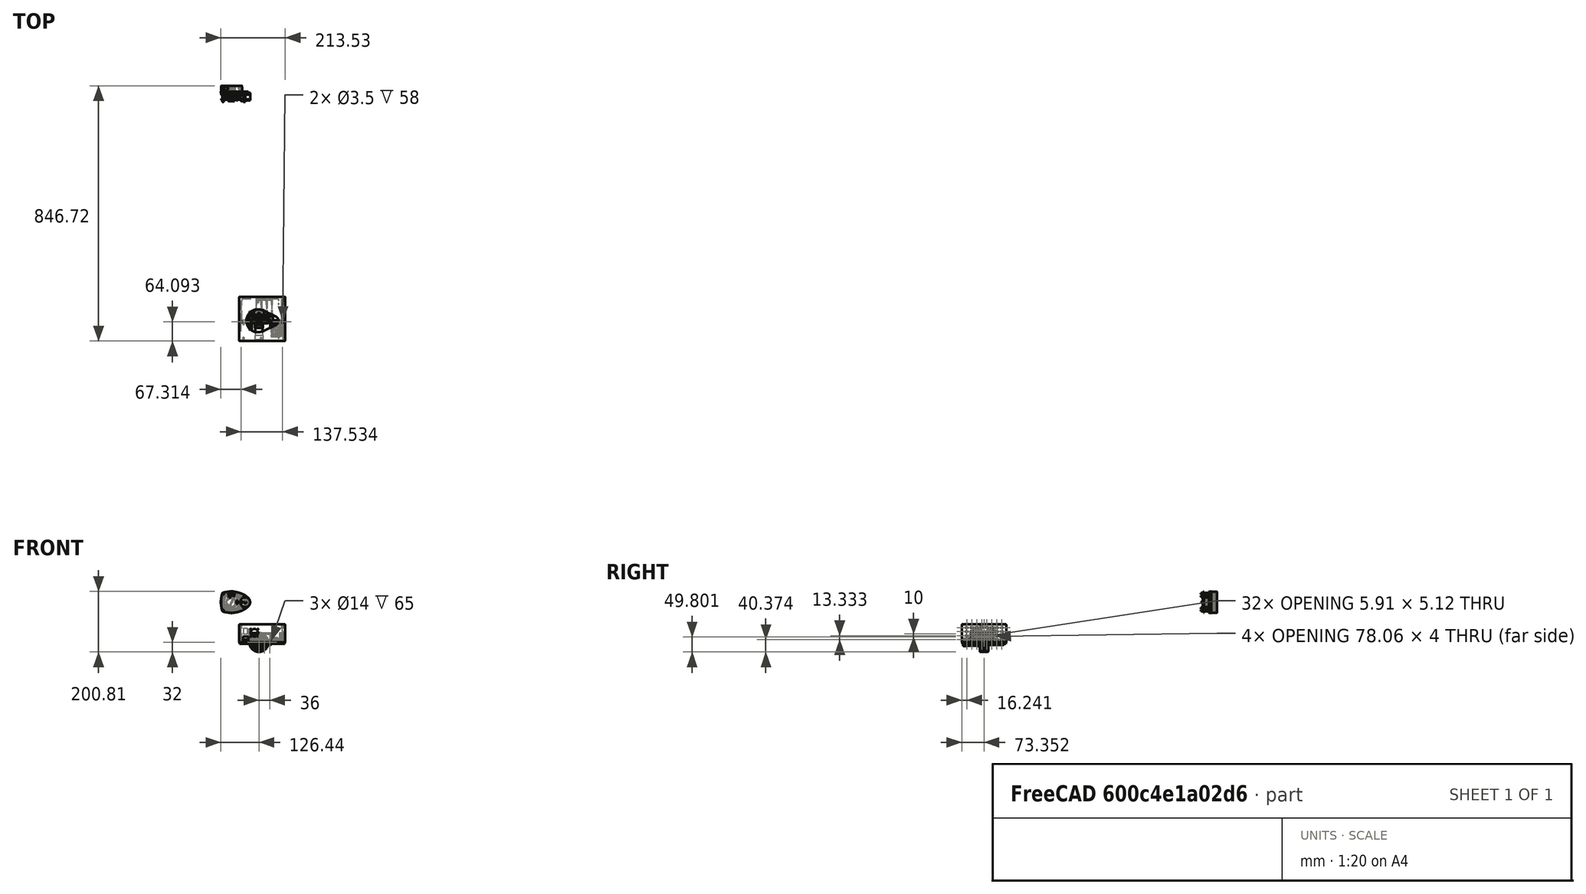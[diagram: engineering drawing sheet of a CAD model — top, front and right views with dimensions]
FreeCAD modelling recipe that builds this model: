
FCSTD DOCUMENT  (FreeCAD 0.20R29603 (Git))
Label: autonomous_bot
License: All rights reserved
LicenseURL: http://en.wikipedia.org/wiki/All_rights_reserved
objects: Part::Feature×53, Sketcher::SketchObject×19, PartDesign::Pad×14, App::Part×13, PartDesign::Pocket×8, PartDesign::Body×4, PartDesign::LinearPattern×3, PartDesign::Fillet×2, PartDesign::MultiTransform×2, Mesh::Feature×1, PartDesign::Plane×1, PartDesign::Thickness×1, PartDesign::Hole×1
note: 134 computed .brp shape members not serialized (recipe doc carries the construction recipe); baked Part::Feature solids carry a one-line shape summary decoded from their .brp

FEATURE [Part::Feature] Part__Feature002  label="cell"
  Placement = pos=(0,0,0) rot=(-1,0,0;1.5708rad)
  shape: bbox 19.5 x 65.01 x 19.5 mm, 44 faces, 4 solids (baked)
FEATURE [Part::Feature] Part__Feature093  label="cell001"
  Placement = pos=(18,0,0) rot=(-1,0,0;1.5708rad)
  shape: bbox 19.5 x 65.01 x 19.5 mm, 44 faces, 4 solids (baked)
FEATURE [Part::Feature] Part__Feature094  label="cell002"
  Placement = pos=(36,0,0) rot=(-1,0,0;1.5708rad)
  shape: bbox 19.5 x 65.01 x 19.5 mm, 44 faces, 4 solids (baked)
FEATURE [Part::Feature] Part__Feature095  label="L298N Motor Driver001"
  Placement = pos=(62,-37,4) rot=(0.57735,0.57735,0.57735;2.0944rad)
  shape: bbox 43.5 x 43.5 x 26 mm, 749 faces, 21 solids (baked)
FEATURE [App::Part] Part002  label="battery"
  Group = -> [Part__Feature094,Part__Feature093,Part__Feature002]
  Origin = -> Origin037
  Placement = pos=(67,23,18) rot=(0,0,1;1.5708rad)
FEATURE [Part::Feature] Part__Feature096  label="1"
  Placement = pos=(0,3,-1e-15) rot=(1,0,0;3.14159rad)
  shape: bbox 27 x 32.5 x 32.1 mm, 22 faces (baked)
FEATURE [Part::Feature] Part__Feature097  label="2"
  Placement = pos=(3e-15,-12,3e-15) rot=(0,0,1;0rad)
  shape: bbox 26.5 x 69.5 x 26.5 mm, 11 faces (baked)
FEATURE [App::Part] _  label="3"
  Group = -> [Part__Feature096,Part__Feature097]
  Origin = -> Origin039
FEATURE [Part::Feature] Part__Feature098  label="4"
  shape: bbox 52 x 26 x 52 mm, 199 faces (baked)
FEATURE [Part::Feature] Part__Feature099  label="5"
  Placement = pos=(-1e-15,0,-4e-15) rot=(0,1,0;0.005059rad)
  shape: bbox 73.6 x 28 x 73.6 mm, 536 faces (baked)
FEATURE [App::Part] _001  label="6"
  Group = -> [Part__Feature098,Part__Feature099]
  Origin = -> Origin040
FEATURE [Part::Feature] Part__Feature100  label="7"
  Placement = pos=(0,-14,0) rot=(0,0,1;0rad)
  shape: bbox 13 x 26 x 15.01 mm, 12 faces (baked)
FEATURE [Part::Feature] Part__Feature101  label="<unrecoverable-encoding: 39 bytes e8eeb0a0f2aca1b1ebb1b3e4... md5=072de469>7045 - ʳ x 6 - H"
  Placement = pos=(4,-22,6.9282) rot=(0.047005,0.995571,-0.081416;2.09823rad)
  shape: bbox 7.624 x 5.981 x 8.776 mm, 28 faces (baked)
FEATURE [Part::Feature] Part__Feature102  label="Âèíò ñ öèëèíäðè÷åñêîé ãîëîâêîé è øåñòèãðàííûì óãëóáëåíèåì ïîä êëþ÷ ÃÎÑÒ Ð ÈÑÎ 4762 - Ì3 x 12"
  Placement = pos=(0,6.5,0) rot=(0,0,-1;1.5708rad)
  shape: bbox 5.953 x 15 x 5.953 mm, 15 faces (baked)
FEATURE [Part::Feature] Part__Feature103  label="10"
  Placement = pos=(0,-31,0) rot=(0,0,1;0rad)
  shape: bbox 4 x 15 x 4 mm, 3 faces (baked)
FEATURE [App::Part] _1  label="11"
  Group = -> [_001,Part__Feature100,Part__Feature101,Part__Feature102,Part__Feature103]
  Origin = -> Origin041
  Placement = pos=(4e-16,31,-6.6e-15) rot=(0,1,0;1.91042rad)
FEATURE [App::Part] Shapes  label="motor_wheel_r"
  Group = -> [_,_1]
  Origin = -> Origin042
  Placement = pos=(71.52,71,-23.51) rot=(0,1,0;6.28318rad)
FEATURE [Mesh::Feature] Raspberry_Pi_4_Model_B_03  label="Raspberry_Pi_4-Model_B-03"
  Placement = pos=(-12,-40,4) rot=(0,0,1;0rad)
FEATURE [Part::Feature] RP_lidar_A1
  Placement = pos=(-90.5533,748.292,132.918) rot=(0,0,1;0rad)
  shape: bbox 114.9 x 12.7 x 93.34 mm, 1511 faces (baked)
FEATURE [Part::Feature] RP_lidar_A1001
  Placement = pos=(-90.5533,751.292,132.918) rot=(0,1,0;0.450629rad)
  shape: bbox 106.3 x 21.41 x 108.5 mm, 315 faces (baked)
FEATURE [Part::Feature] RP_lidar_A1002
  Placement = pos=(-90.4238,754.292,132.776) rot=(0,1,0;2.02364rad)
  shape: bbox 32 x 21.09 x 28.13 mm, 95 faces (baked)
FEATURE [Part::Feature] RP_lidar_A1003
  Placement = pos=(-93.3269,763.292,153.094) rot=(-0.486868,-0.396432,0.778332;2.01185rad)
  shape: bbox 17.19 x 18.52 x 19.42 mm, 10 faces (baked)
FEATURE [Part::Feature] RP_lidar_A1004
  Placement = pos=(-96.1268,764.292,107.826) rot=(-0.316381,-0.743803,0.588778;1.25125rad)
  shape: bbox 22.76 x 9.219 x 19.38 mm, 14 faces (baked)
FEATURE [Part::Feature] RP_lidar_A1005
  Placement = pos=(-90.5533,755.292,132.918) rot=(0,1,0;2.01581rad)
  shape: bbox 22.94 x 18.5 x 22.57 mm, 35 faces (baked)
FEATURE [Part::Feature] RP_lidar_A1006
  Placement = pos=(-90.5533,773.192,132.918) rot=(0.847211,0,0.531257;3.14159rad)
  shape: bbox 106.3 x 19.54 x 108.3 mm, 453 faces (baked)
FEATURE [Part::Feature] RP_lidar_A1007
  Placement = pos=(-64.2029,766.792,142.386) rot=(0.652395,-0.652395,-0.385697;2.40536rad)
  shape: bbox 5.324 x 7.569 x 5.324 mm, 18 faces (baked)
FEATURE [Part::Feature] RP_lidar_A1008
  Placement = pos=(-81.6242,766.792,106.379) rot=(0.652395,-0.652395,-0.385697;2.40536rad)
  shape: bbox 5.324 x 7.569 x 5.324 mm, 18 faces (baked)
FEATURE [Part::Feature] RP_lidar_A1009
  Placement = pos=(-115.758,766.792,145.112) rot=(0.639808,-0.639808,-0.425783;2.33652rad)
  shape: bbox 5.13 x 7.569 x 5.13 mm, 18 faces (baked)
FEATURE [Part::Feature] RP_lidar_A1010
  Placement = pos=(-90.5533,738.292,132.918) rot=(0,0,1;0rad)
  shape: bbox 55.52 x 1.02 x 57.02 mm, 27 faces (baked)
FEATURE [Part::Feature] RP_lidar_A1011
  Placement = pos=(-57.5533,723.492,132.555) rot=(0.57735,-0.57735,0.57735;2.0944rad)
  shape: bbox 5.22 x 3.42 x 8.92 mm, 221 faces (baked)
FEATURE [Part::Feature] RP_lidar_A1012
  Placement = pos=(-45.0533,728.792,132.918) rot=(0,-1,0;1.5708rad)
  shape: bbox 32 x 30.2 x 32.81 mm, 39 faces (baked)
FEATURE [Part::Feature] RP_lidar_A1013
  Placement = pos=(-45.0533,725.192,132.918) rot=(0,-1,0;1.13719rad)
  shape: bbox 42.51 x 1.6 x 42.51 mm, 4 faces (baked)
FEATURE [Part::Feature] RP_lidar_A1014
  Placement = pos=(-45.0533,750.592,121.918) rot=(-0.016461,0.016461,-0.999729;1.57107rad)
  shape: bbox 4.047 x 7.569 x 4.047 mm, 18 faces (baked)
FEATURE [Part::Feature] RP_lidar_A1015
  Placement = pos=(-45.0533,750.592,143.918) rot=(-0.016461,0.016461,-0.999729;1.57107rad)
  shape: bbox 4.047 x 7.569 x 4.047 mm, 18 faces (baked)
FEATURE [Part::Feature] RP_lidar_A1016
  Placement = pos=(-68.3533,736.442,132.793) rot=(0.707107,0,0.707107;3.14159rad)
  shape: bbox 4.72 x 4.22 x 10.17 mm, 257 faces (baked)
FEATURE [Part::Feature] RP_lidar_A1017
  Placement = pos=(-90.5533,737.292,132.918) rot=(0,0,1;0rad)
  shape: bbox 60.22 x 11.07 x 60.95 mm, 180 faces (baked)
FEATURE [Part::Feature] RP_lidar_A1018
  Placement = pos=(-118.553,729.292,160.918) rot=(0,0,1;0rad)
  shape: bbox 5.794 x 15.02 x 5.02 mm, 9 faces (baked)
FEATURE [Part::Feature] RP_lidar_A1019
  Placement = pos=(-48.5533,727.692,152.918) rot=(1,0,0;3.14159rad)
  shape: bbox 5.794 x 8.02 x 5.02 mm, 9 faces (baked)
FEATURE [Part::Feature] RP_lidar_A1020
  Placement = pos=(-48.5533,729.292,152.918) rot=(0,0,1;0rad)
  shape: bbox 5.794 x 15.02 x 5.02 mm, 9 faces (baked)
FEATURE [Part::Feature] RP_lidar_A1021
  Placement = pos=(-118.553,727.692,160.918) rot=(1,0,0;3.14159rad)
  shape: bbox 5.794 x 8.02 x 5.02 mm, 9 faces (baked)
FEATURE [Part::Feature] RP_lidar_A1022
  Placement = pos=(-48.5533,729.292,112.918) rot=(0,0,1;0rad)
  shape: bbox 5.794 x 15.02 x 5.02 mm, 9 faces (baked)
FEATURE [Part::Feature] RP_lidar_A1023
  Placement = pos=(-118.553,727.692,104.918) rot=(1,0,0;3.14159rad)
  shape: bbox 5.794 x 8.02 x 5.02 mm, 9 faces (baked)
FEATURE [Part::Feature] RP_lidar_A1024
  Placement = pos=(-118.553,729.292,104.918) rot=(0,0,1;0rad)
  shape: bbox 5.794 x 15.02 x 5.02 mm, 9 faces (baked)
FEATURE [Part::Feature] RP_lidar_A1025
  Placement = pos=(-48.5533,727.692,112.918) rot=(1,0,0;3.14159rad)
  shape: bbox 5.794 x 8.02 x 5.02 mm, 9 faces (baked)
FEATURE [Part::Feature] RP_lidar_A1026
  Placement = pos=(-90.5533,727.692,160.018) rot=(0.57735,-0.57735,0.57735;4.18879rad)
  shape: bbox 20.02 x 8.21 x 5.02 mm, 42 faces (baked)
FEATURE [Part::Feature] RP_lidar_A1027
  Placement = pos=(-90.5533,729.292,132.918) rot=(1,0,0;3.14159rad)
  shape: bbox 85.12 x 214.2 x 70.02 mm, 368 faces (baked)
FEATURE [Part::Feature] RP_lidar_A1028
  Placement = pos=(-90.5533,751.478,132.918) rot=(1,0,0;1.5708rad)
  shape: bbox 103.2 x 2 x 95.72 mm, 4 faces (baked)
FEATURE [Part::Feature] RP_lidar_A1029
  Placement = pos=(-45.0533,749.292,132.918) rot=(0,1,0;1.69522rad)
  shape: bbox 20.12 x 5.5 x 20.12 mm, 19 faces (baked)
FEATURE [App::Part] Part003  label="RPILIDAR"
  Group = -> [RP_lidar_A1,RP_lidar_A1001,RP_lidar_A1002,RP_lidar_A1003,RP_lidar_A1004,RP_lidar_A1005,RP_lidar_A1006,RP_lidar_A1007,RP_lidar_A1008,RP_lidar_A1009,RP_lidar_A1010,RP_lidar_A1011,RP_lidar_A1012,RP_lidar_A1013,RP_lidar_A1014,RP_lidar_A1015,RP_lidar_A1016,RP_lidar_A1017,RP_lidar_A1018,RP_lidar_A1019,RP_lidar_A1020,RP_lidar_A1021,RP_lidar_A1022,RP_lidar_A1023,RP_lidar_A1024,RP_lidar_A1025,+4 more]
  Origin = -> Origin038
  Placement = pos=(90,127,-691) rot=(1,0,0;1.5708rad)
FEATURE [Part::Feature] Part__Feature104  label="1002"
  Placement = pos=(0,3,-1e-15) rot=(1,0,0;3.14159rad)
  shape: bbox 27 x 32.5 x 32.1 mm, 22 faces (baked)
FEATURE [Part::Feature] Part__Feature105  label="2001"
  Placement = pos=(3e-15,-12,3e-15) rot=(0,0,1;0rad)
  shape: bbox 26.5 x 69.5 x 26.5 mm, 11 faces (baked)
FEATURE [Part::Feature] Part__Feature106  label="4001"
  shape: bbox 52 x 26 x 52 mm, 199 faces (baked)
FEATURE [Part::Feature] Part__Feature107  label="5001"
  Placement = pos=(-1e-15,0,-4e-15) rot=(0,1,0;0.005059rad)
  shape: bbox 73.6 x 28 x 73.6 mm, 536 faces (baked)
FEATURE [Part::Feature] Part__Feature108  label="7001"
  Placement = pos=(0,-14,0) rot=(0,0,1;0rad)
  shape: bbox 13 x 26 x 15.01 mm, 12 faces (baked)
FEATURE [Part::Feature] Part__Feature109  label="<unrecoverable-encoding: 39 bytes e8eeb0a0f2aca1b1ebb1b3e4... md5=072de469>7045 - ʳ x 6 - H001"
  Placement = pos=(4,-22,6.9282) rot=(0.047005,0.995571,-0.081416;2.09823rad)
  shape: bbox 7.624 x 5.981 x 8.776 mm, 28 faces (baked)
FEATURE [Part::Feature] Part__Feature110  label="Âèíò ñ öèëèíäðè÷åñêîé ãîëîâêîé è øåñòèãðàííûì óãëóáëåíèåì ïîä êëþ÷ ÃÎÑÒ Ð ÈÑÎ 4762 - Ì3 x 013"
  Placement = pos=(0,6.5,0) rot=(0,0,-1;1.5708rad)
  shape: bbox 5.953 x 15 x 5.953 mm, 15 faces (baked)
FEATURE [Part::Feature] Part__Feature111  label="10003"
  Placement = pos=(0,-31,0) rot=(0,0,1;0rad)
  shape: bbox 4 x 15 x 4 mm, 3 faces (baked)
FEATURE [App::Part] _002  label="3001"
  Group = -> [Part__Feature104,Part__Feature105]
  Origin = -> Origin043
FEATURE [App::Part] _003  label="6001"
  Group = -> [Part__Feature106,Part__Feature107]
  Origin = -> Origin044
FEATURE [App::Part] _004  label="11001"
  Group = -> [_003,Part__Feature108,Part__Feature109,Part__Feature110,Part__Feature111]
  Origin = -> Origin045
  Placement = pos=(4e-16,31,-6.6e-15) rot=(0,1,0;1.91042rad)
FEATURE [App::Part] Shapes001  label="motor_wheel_l"
  Group = -> [_002,_004]
  Origin = -> Origin046
  Placement = pos=(71,-71,-24.27) rot=(0,0,-1;3.14159rad)
FEATURE [Sketcher::SketchObject] Sketch
  FullyConstrained = true
  MapMode = 5
  Support = -> [XY_Plane048]
  sketch-geometry (4):
    g0: LineSegment StartX=-75 StartY=72.5 StartZ=0 EndX=75 EndY=72.5 EndZ=0
    g1: LineSegment StartX=75 StartY=72.5 StartZ=0 EndX=75 EndY=-72.5 EndZ=0
    g2: LineSegment StartX=75 StartY=-72.5 StartZ=0 EndX=-75 EndY=-72.5 EndZ=0
    g3: LineSegment StartX=-75 StartY=-72.5 StartZ=0 EndX=-75 EndY=72.5 EndZ=0
  constraints (11):
    c: Coincident(g0,g1)
    c: Coincident(g1,g2)
    c: Coincident(g2,g3)
    c: Coincident(g3,g0)
    c: Horizontal(g0)
    c: Horizontal(g2)
    c: Vertical(g1)
    c: Vertical(g3)
    c: Symmetric(g1,g0,g-1)
    c: DistanceX(g0,g0) = 150
    c: DistanceY(g1,g1) = 145
FEATURE [Part::Feature] Part__Feature112  label="Caster_40mm_Wheel_30mm_01"
  shape: bbox 15.6 x 30 x 30 mm, 12 faces (baked)
FEATURE [Part::Feature] Part__Feature113  label="Caster_40mm_Wheel_support_01"
  shape: bbox 25.52 x 33.35 x 25.15 mm, 56 faces (baked)
FEATURE [Part::Feature] Part__Feature114  label="Caster_40mm_Swivel_plate_01"
  shape: bbox 38 x 33.34 x 8.3 mm, 30 faces (baked)
FEATURE [App::Part] Part004  label="Caster Wheel"
  Group = -> [Part__Feature112,Part__Feature113,Part__Feature114]
  Origin = -> Origin049
  Placement = pos=(-33,-1,-42) rot=(0,0,1;1.5708rad)
FEATURE [PartDesign::Pad] Pad
  Direction = (0,0,1)
  Length = 5
  Length2 = 10
  Profile = -> Sketch
  ReferenceAxis = -> Sketch [N_Axis]
  Reversed = true
  Type = 0
FEATURE [Sketcher::SketchObject] Sketch001
  ExternalGeometry = -> [Pad]
  FullyConstrained = false
  MapMode = 5
  Support = -> [Pad]
  sketch-geometry (8):
    g0: Circle CenterX=54 CenterY=63.26 CenterZ=0 NormalX=0 NormalY=0 NormalZ=1 AngleXU=0 Radius=1.51945
    g1: Circle CenterX=69 CenterY=63.26 CenterZ=0 NormalX=0 NormalY=0 NormalZ=1 AngleXU=0 Radius=1.57564
    g2: Circle CenterX=69 CenterY=49.76 CenterZ=0 NormalX=0 NormalY=0 NormalZ=1 AngleXU=0 Radius=1.58481
    g3: Circle CenterX=54 CenterY=49.76 CenterZ=0 NormalX=0 NormalY=0 NormalZ=1 AngleXU=0 Radius=1.46067
    g4: Circle CenterX=54 CenterY=-49.76 CenterZ=0 NormalX=0 NormalY=0 NormalZ=1 AngleXU=0 Radius=1.51945
    g5: Circle CenterX=69 CenterY=-49.76 CenterZ=0 NormalX=0 NormalY=0 NormalZ=1 AngleXU=0 Radius=1.57564
    g6: Circle CenterX=69 CenterY=-63.26 CenterZ=0 NormalX=0 NormalY=0 NormalZ=1 AngleXU=0 Radius=1.58481
    g7: Circle CenterX=54 CenterY=-63.26 CenterZ=0 NormalX=0 NormalY=0 NormalZ=1 AngleXU=0 Radius=1.46067
  constraints (16):
    c: DistanceX(g3,g2) = 15
    c: Vertical(g3,g0)
    c: Horizontal(g2,g3)
    c: Vertical(g2,g1)
    c: DistanceY(g3,g0) = 13.5
    c: DistanceX(g1,g-3) = 6
    c: Horizontal(g0,g1)
    c: DistanceX(g7,g6) = 15
    c: Vertical(g7,g4)
    c: Horizontal(g6,g7)
    c: Vertical(g6,g5)
    c: DistanceY(g7,g4) = 13.5
    c: Horizontal(g4,g5)
    c: Vertical(g5,g2)
    c: DistanceY(g1,g-3) = 9.24
    c: DistanceY(g-4,g6) = 9.24
FEATURE [PartDesign::Pocket] Pocket
  BaseFeature = -> Pad
  Direction = (0,0,-1)
  Length = 5
  Length2 = 5
  Profile = -> Sketch001
  ReferenceAxis = -> Sketch001 [N_Axis]
  Type = 0
FEATURE [Sketcher::SketchObject] Sketch002
  FullyConstrained = false
  MapMode = 5
  Support = -> [XY_Plane050]
  sketch-geometry (4):
    g0: LineSegment StartX=-66.2084 StartY=72.1684 StartZ=0 EndX=63.7916 EndY=72.1684 EndZ=0
    g1: LineSegment StartX=63.7916 StartY=72.1684 StartZ=0 EndX=63.7916 EndY=1.16836 EndZ=0
    g2: LineSegment StartX=63.7916 StartY=1.16836 StartZ=0 EndX=-66.2084 EndY=1.16836 EndZ=0
    g3: LineSegment StartX=-66.2084 StartY=1.16836 StartZ=0 EndX=-66.2084 EndY=72.1684 EndZ=0
  constraints (10):
    c: Coincident(g0,g1)
    c: Coincident(g1,g2)
    c: Coincident(g2,g3)
    c: Coincident(g3,g0)
    c: Horizontal(g0)
    c: Horizontal(g2)
    c: Vertical(g1)
    c: Vertical(g3)
    c: DistanceY(g1,g1) = 71
    c: DistanceX(g0,g0) = 130
FEATURE [PartDesign::Pad] Pad001
  Direction = (0,0,1)
  Length = 9
  Length2 = 10
  Profile = -> Sketch002
  ReferenceAxis = -> Sketch002 [N_Axis]
  Type = 0
FEATURE [PartDesign::Fillet] Fillet
  Base = -> Pad001 [Edge9,Edge10,Edge4,Edge3]
  BaseFeature = -> Pad001
  Radius = 4
  SupportTransform = false
  UseAllEdges = false
FEATURE [PartDesign::Body] Body002  label="Power_bank"
  Group = -> [Sketch002,Pad001,Fillet]
  Origin = -> Origin050
  Placement = pos=(10,-6,0) rot=(0,0,1;0rad)
  Tip = -> Fillet
FEATURE [App::Part] Part001  label="Components"
  Group = -> [Part__Feature095,Part002,Shapes,Raspberry_Pi_4_Model_B_03,Part003,Shapes001,Part004,Body002]
  Origin = -> Origin036
FEATURE [Sketcher::SketchObject] Sketch003
  FullyConstrained = false
  MapMode = 5
  Support = -> [Pocket]
  sketch-geometry (16):
    g0: Circle CenterX=69.7676 CenterY=-18.2699 CenterZ=0 NormalX=0 NormalY=0 NormalZ=1 AngleXU=0 Radius=1.5
    g1: Circle CenterX=69.7676 CenterY=-18.2699 CenterZ=0 NormalX=0 NormalY=0 NormalZ=1 AngleXU=0 Radius=3
    g2: Circle CenterX=32.2561 CenterY=-18.2919 CenterZ=0 NormalX=0 NormalY=0 NormalZ=1 AngleXU=0 Radius=1.5
    g3: Circle CenterX=32.2561 CenterY=-18.2919 CenterZ=0 NormalX=0 NormalY=0 NormalZ=1 AngleXU=0 Radius=3
    g4: Circle CenterX=32.2849 CenterY=-55.7579 CenterZ=0 NormalX=0 NormalY=0 NormalZ=1 AngleXU=0 Radius=1.5
    g5: Circle CenterX=32.2849 CenterY=-55.7579 CenterZ=0 NormalX=0 NormalY=0 NormalZ=1 AngleXU=0 Radius=3
    g6: Circle CenterX=69.7365 CenterY=-55.7732 CenterZ=0 NormalX=0 NormalY=0 NormalZ=1 AngleXU=0 Radius=1.5
    g7: Circle CenterX=69.7365 CenterY=-55.7732 CenterZ=0 NormalX=0 NormalY=0 NormalZ=1 AngleXU=0 Radius=3
    g8: Circle CenterX=-62.0545 CenterY=-15.516 CenterZ=0 NormalX=0 NormalY=0 NormalZ=1 AngleXU=0 Radius=1.5
    g9: Circle CenterX=-62.0545 CenterY=-15.516 CenterZ=0 NormalX=0 NormalY=0 NormalZ=1 AngleXU=0 Radius=3
    g10: Circle CenterX=-4.04448 CenterY=-15.6135 CenterZ=0 NormalX=0 NormalY=0 NormalZ=1 AngleXU=0 Radius=1.5
    g11: Circle CenterX=-4.04448 CenterY=-15.6135 CenterZ=0 NormalX=0 NormalY=0 NormalZ=1 AngleXU=0 Radius=3
    g12: Circle CenterX=-4.04448 CenterY=-64.6735 CenterZ=0 NormalX=0 NormalY=0 NormalZ=1 AngleXU=0 Radius=1.5
    g13: Circle CenterX=-4.04448 CenterY=-64.6735 CenterZ=0 NormalX=0 NormalY=0 NormalZ=1 AngleXU=0 Radius=3
    g14: Circle CenterX=-62.0645 CenterY=-64.556 CenterZ=0 NormalX=0 NormalY=0 NormalZ=1 AngleXU=0 Radius=1.5
    g15: Circle CenterX=-62.0645 CenterY=-64.556 CenterZ=0 NormalX=0 NormalY=0 NormalZ=1 AngleXU=0 Radius=3
  constraints (22):
    c: Coincident(g1,g0)
    c: Diameter(g0) = 3
    c: Coincident(g3,g2)
    c: Equal(g0,g2) = 3
    c: Equal(g1,g3) = 5
    c: Coincident(g5,g4)
    c: Coincident(g7,g6)
    c: Coincident(g9,g8)
    c: Coincident(g11,g10)
    c: Coincident(g13,g12)
    c: Coincident(g15,g14)
    c: Diameter(g11) = 6
    c: Equal(g11,g9)
    c: Equal(g9,g13)
    c: Equal(g13,g5)
    c: Equal(g5,g7)
    c: Equal(g7,g1)
    c: Equal(g1,g15)
    c: DistanceX(g8,g10) = 58.01
    c: DistanceX(g14,g12) = 58.02
    c: DistanceY(g14,g8) = 49.04
    c: DistanceY(g12,g10) = 49.06
FEATURE [PartDesign::Pad] Pad002
  BaseFeature = -> Pocket
  Direction = (0,0,1)
  Length = 5
  Length2 = 10
  Profile = -> Sketch003
  ReferenceAxis = -> Sketch003 [N_Axis]
  Type = 0
FEATURE [Sketcher::SketchObject] Sketch004
  FullyConstrained = false
  MapMode = 5
  Support = -> [Pad002]
  sketch-geometry (16):
    g0: LineSegment StartX=71.0615 StartY=32.7631 StartZ=0 EndX=66.0615 EndY=32.7631 EndZ=0
    g1: LineSegment StartX=66.0615 StartY=32.7631 StartZ=0 EndX=66.0615 EndY=7.76305 EndZ=0
    g2: LineSegment StartX=66.0615 StartY=7.76305 StartZ=0 EndX=71.0615 EndY=7.76305 EndZ=0
    g3: LineSegment StartX=71.0615 StartY=7.76305 StartZ=0 EndX=71.0615 EndY=32.7631 EndZ=0
    g4: LineSegment StartX=-68.8319 StartY=57.641 StartZ=0 EndX=-73.8319 EndY=57.641 EndZ=0
    g5: LineSegment StartX=-73.8319 StartY=57.641 StartZ=0 EndX=-73.8319 EndY=32.641 EndZ=0
    g6: LineSegment StartX=-73.8319 StartY=32.641 StartZ=0 EndX=-68.8319 EndY=32.641 EndZ=0
    g7: LineSegment StartX=-68.8319 StartY=32.641 StartZ=0 EndX=-68.8319 EndY=57.641 EndZ=0
    g8: LineSegment StartX=-18.4487 StartY=70.9815 StartZ=0 EndX=11.5513 EndY=70.9815 EndZ=0
    g9: LineSegment StartX=11.5513 StartY=70.9815 StartZ=0 EndX=11.5513 EndY=67.9815 EndZ=0
    g10: LineSegment StartX=11.5513 StartY=67.9815 StartZ=0 EndX=-18.4487 EndY=67.9815 EndZ=0
    g11: LineSegment StartX=-18.4487 StartY=67.9815 StartZ=0 EndX=-18.4487 EndY=70.9815 EndZ=0
    g12: LineSegment StartX=-18.4487 StartY=-8.98019 StartZ=0 EndX=11.5513 EndY=-8.98019 EndZ=0
    g13: LineSegment StartX=11.5513 StartY=-8.98019 StartZ=0 EndX=11.5513 EndY=-5.98019 EndZ=0
    g14: LineSegment StartX=11.5513 StartY=-5.98019 StartZ=0 EndX=-18.4487 EndY=-5.98019 EndZ=0
    g15: LineSegment StartX=-18.4487 StartY=-5.98019 StartZ=0 EndX=-18.4487 EndY=-8.98019 EndZ=0
  constraints (41):
    c: Coincident(g0,g1)
    c: Coincident(g1,g2)
    c: Coincident(g2,g3)
    c: Coincident(g3,g0)
    c: Horizontal(g0)
    c: Horizontal(g2)
    c: Vertical(g1)
    c: Vertical(g3)
    c: Coincident(g4,g5)
    c: Coincident(g5,g6)
    c: Coincident(g6,g7)
    c: Coincident(g7,g4)
    c: Horizontal(g4)
    c: Horizontal(g6)
    c: Vertical(g5)
    c: Vertical(g7)
    c: Coincident(g8,g9)
    c: Coincident(g9,g10)
    c: Coincident(g10,g11)
    c: Coincident(g11,g8)
    c: Horizontal(g8)
    c: Horizontal(g10)
    c: Vertical(g9)
    c: Vertical(g11)
    c: Coincident(g12,g13)
    c: Coincident(g13,g14)
    c: Coincident(g14,g15)
    c: Coincident(g15,g12)
    c: Horizontal(g12)
    c: Horizontal(g14)
    c: Vertical(g13)
    c: Vertical(g15)
    c: DistanceX(g0,g0) = 5
    c: DistanceY(g3,g3) = 25
    c: Equal(g3,g7)
    c: Equal(g0,g6)
    c: DistanceY(g9,g9) = 3
    c: DistanceX(g8,g8) = 30
    c: Equal(g10,g14)
    c: Equal(g13,g9)
    c: Vertical(g14,g10)
FEATURE [PartDesign::Pad] Pad003
  BaseFeature = -> Pad002
  Direction = (0,0,1)
  Length = 10
  Length2 = 10
  Profile = -> Sketch004
  ReferenceAxis = -> Sketch004 [N_Axis]
  Type = 3
  UpToFace = -> Fillet [Face10]
FEATURE [Sketcher::SketchObject] Sketch005
  FullyConstrained = false
  MapMode = 5
  Support = -> [Pad003]
  sketch-geometry (11):
    g0: LineSegment StartX=-36.53 StartY=-5.68003 StartZ=0 EndX=-43.53 EndY=-5.68003 EndZ=0
    g1: LineSegment StartX=-43.53 StartY=-5.68003 StartZ=0 EndX=-43.53 EndY=-10.68 EndZ=0
    g2: LineSegment StartX=-43.53 StartY=-10.68 StartZ=0 EndX=-36.53 EndY=-10.68 EndZ=0
    g3: LineSegment StartX=-36.53 StartY=-10.68 StartZ=0 EndX=-36.53 EndY=-5.68003 EndZ=0
    g4: Circle CenterX=-39.53 CenterY=22.13 CenterZ=0 NormalX=0 NormalY=0 NormalZ=1 AngleXU=0 Radius=1
    g5: Circle CenterX=-39.5108 CenterY=-34.2545 CenterZ=0 NormalX=0 NormalY=0 NormalZ=1 AngleXU=0 Radius=3.53196
    g6: LineSegment StartX=34.49 StartY=-5.68003 StartZ=0 EndX=27.49 EndY=-5.68003 EndZ=0
    g7: LineSegment StartX=27.49 StartY=-5.68003 StartZ=0 EndX=27.49 EndY=-10.68 EndZ=0
    g8: LineSegment StartX=27.49 StartY=-10.68 StartZ=0 EndX=34.49 EndY=-10.68 EndZ=0
    g9: LineSegment StartX=34.49 StartY=-10.68 StartZ=0 EndX=34.49 EndY=-5.68003 EndZ=0
    g10: Circle CenterX=30.49 CenterY=14.06 CenterZ=0 NormalX=0 NormalY=0 NormalZ=1 AngleXU=0 Radius=1
  constraints (29):
    c: Coincident(g0,g1)
    c: Coincident(g1,g2)
    c: Coincident(g2,g3)
    c: Coincident(g3,g0)
    c: Horizontal(g0)
    c: Horizontal(g2)
    c: Vertical(g1)
    c: Vertical(g3)
    c: DistanceY(g1,g1) = 5
    c: DistanceX(g2,g2) = 7
    c: DistanceX(g0,g4) = 4
    c: Coincident(g6,g7)
    c: Coincident(g7,g8)
    c: Coincident(g8,g9)
    c: Coincident(g9,g6)
    c: Horizontal(g6)
    c: Horizontal(g8)
    c: Vertical(g7)
    c: Vertical(g9)
    c: Equal(g1,g7) = 5
    c: Equal(g2,g8) = 7
    c: Diameter(g10) = 2
    c: Diameter(g4) = 2
    c: DistanceX(g10) = 30.49
    c: DistanceY(g-1,g10) = 14.06
    c: DistanceY(g-1,g4) = 22.13
    c: DistanceX(g4,g-1) = 39.53
    c: DistanceX(g10,g6) = 4
    c: Horizontal(g0,g6)
FEATURE [PartDesign::Pad] Pad004
  BaseFeature = -> Pad003
  Direction = (0,0,1)
  Length = 27
  Length2 = 10
  Profile = -> Sketch005
  ReferenceAxis = -> Sketch005 [N_Axis]
  Type = 0
FEATURE [PartDesign::Plane] DatumPlane
  AttachmentOffset = pos=(0,0,27) rot=(0,0,1;0rad)
  Length = 93.5905
  MapMode = 5
  Placement = pos=(0,0,27) rot=(0,0,1;0rad)
  ResizeMode = 0
  Support = -> [XY_Plane051]
  Width = 79.2542
FEATURE [Sketcher::SketchObject] Sketch006
  FullyConstrained = false
  MapMode = 5
  Placement = pos=(0,0,27) rot=(0,0,1;0rad)
  Support = -> [DatumPlane]
  sketch-geometry (14):
    g0: LineSegment StartX=46.4839 StartY=18.7471 StartZ=0 EndX=37.4839 EndY=18.7471 EndZ=0
    g1: LineSegment StartX=37.4839 StartY=18.7471 StartZ=0 EndX=37.4839 EndY=5.11021 EndZ=0
    g2: LineSegment StartX=37.4839 StartY=-31.2529 StartZ=0 EndX=46.4839 EndY=-31.2529 EndZ=0
    g3: LineSegment StartX=46.4839 StartY=-31.2529 StartZ=0 EndX=46.4839 EndY=18.7471 EndZ=0
    g4: LineSegment StartX=-32.7624 StartY=26.6397 StartZ=0 EndX=-23.7624 EndY=26.6397 EndZ=0
    g5: LineSegment StartX=-23.7624 StartY=26.6397 StartZ=0 EndX=-23.7624 EndY=5.11021 EndZ=0
    g6: LineSegment StartX=-23.7624 StartY=-38.2703 StartZ=0 EndX=-32.7624 EndY=-38.2703 EndZ=0
    g7: LineSegment StartX=-32.7624 StartY=-38.2703 StartZ=0 EndX=-32.7624 EndY=26.6397 EndZ=0
    g8: Circle CenterX=41.882 CenterY=-8.31986 CenterZ=0 NormalX=0 NormalY=0 NormalZ=1 AngleXU=0 Radius=1.5
    g9: Circle CenterX=-29.0721 CenterY=-8.14094 CenterZ=0 NormalX=0 NormalY=0 NormalZ=1 AngleXU=0 Radius=1.5
    g10: LineSegment StartX=-23.7624 StartY=-12.9501 StartZ=0 EndX=37.4876 EndY=-12.9501 EndZ=0
    g11: LineSegment StartX=37.4839 StartY=5.11021 StartZ=0 EndX=-23.7624 EndY=5.11021 EndZ=0
    g12: LineSegment StartX=-23.7624 StartY=-12.9501 StartZ=0 EndX=-23.7624 EndY=-38.2703 EndZ=0
    g13: LineSegment StartX=37.4876 StartY=-12.9501 StartZ=0 EndX=37.4839 EndY=-31.2529 EndZ=0
  constraints (31):
    c: Coincident(g0,g1)
    c: Coincident(g13,g2)
    c: Coincident(g2,g3)
    c: Coincident(g3,g0)
    c: Horizontal(g0)
    c: Horizontal(g2)
    c: Vertical(g1)
    c: Vertical(g3)
    c: Coincident(g4,g5)
    c: Coincident(g12,g6)
    c: Coincident(g6,g7)
    c: Coincident(g7,g4)
    c: Horizontal(g4)
    c: Horizontal(g6)
    c: Vertical(g5)
    c: Vertical(g7)
    c: DistanceX(g2,g2) = 9
    c: DistanceY(g3,g3) = 50
    c: Diameter(g8) = 3
    c: DistanceX(g6,g6) = 9
    c: Diameter(g9) = 3
    c: Horizontal(g10)
    c: Horizontal(g11)
    c: Coincident(g5,g11)
    c: Coincident(g12,g10)
    c: Coincident(g1,g11)
    c: Coincident(g13,g10)
    c: DistanceY(g7,g7) = 64.91
    c: DistanceX(g10,g10) = 61.25
    c: DistanceX(g4,g4) = 9
    c: DistanceX(g0,g0) = 9
FEATURE [PartDesign::Pad] Pad005
  Direction = (0,0,1)
  Length = 4
  Length2 = 10
  Placement = pos=(0,0,27) rot=(0,0,1;0rad)
  Profile = -> Sketch006
  ReferenceAxis = -> Sketch006 [N_Axis]
  Type = 0
FEATURE [Sketcher::SketchObject] Sketch007
  FullyConstrained = false
  MapMode = 5
  Placement = pos=(0,0,31) rot=(0,0,1;0rad)
  Support = -> [Pad005]
  sketch-geometry (8):
    g0: Circle CenterX=41.4592 CenterY=-25.8844 CenterZ=0 NormalX=0 NormalY=0 NormalZ=1 AngleXU=0 Radius=3.5
    g1: Circle CenterX=41.4216 CenterY=14.0673 CenterZ=0 NormalX=0 NormalY=0 NormalZ=1 AngleXU=0 Radius=3.5
    g2: Circle CenterX=-28.5461 CenterY=-33.9088 CenterZ=0 NormalX=0 NormalY=0 NormalZ=1 AngleXU=0 Radius=3.5
    g3: Circle CenterX=-28.5459 CenterY=22.1831 CenterZ=0 NormalX=0 NormalY=0 NormalZ=1 AngleXU=0 Radius=3.5
    g4: LineSegment StartX=36.4007 StartY=-10.8513 StartZ=0 EndX=29.0878 EndY=-10.8513 EndZ=0
    g5: LineSegment StartX=29.0878 StartY=-10.8513 StartZ=0 EndX=29.0878 EndY=0.366678 EndZ=0
    g6: LineSegment StartX=29.0878 StartY=0.366678 StartZ=0 EndX=36.4007 EndY=0.366678 EndZ=0
    g7: LineSegment StartX=36.4007 StartY=0.366678 StartZ=0 EndX=36.4007 EndY=-10.8513 EndZ=0
  constraints (12):
    c: Coincident(g4,g5)
    c: Coincident(g5,g6)
    c: Coincident(g6,g7)
    c: Coincident(g7,g4)
    c: Horizontal(g4)
    c: Horizontal(g6)
    c: Vertical(g5)
    c: Vertical(g7)
    c: Diameter(g0) = 7
    c: Equal(g0,g1)
    c: Equal(g1,g3)
    c: Equal(g3,g2)
FEATURE [PartDesign::Pocket] Pocket001
  BaseFeature = -> Pad005
  Direction = (0,0,-1)
  Length = 3
  Length2 = 5
  Placement = pos=(0,0,27) rot=(0,0,1;0rad)
  Profile = -> Sketch007
  ReferenceAxis = -> Sketch007 [N_Axis]
  Type = 0
FEATURE [PartDesign::Body] Body003  label="rpi_lidar_holer"
  Group = -> [DatumPlane,Sketch006,Pad005,Sketch007,Pocket001]
  Origin = -> Origin051
  Tip = -> Pocket001
FEATURE [PartDesign::Pad] Pad006
  BaseFeature = -> Pad004
  Direction = (0,0,1)
  Length = 17
  Length2 = 10
  Profile = -> Pad003 [Face49]
  Type = 0
FEATURE [Sketcher::SketchObject] Sketch008
  FullyConstrained = false
  MapMode = 5
  Placement = pos=(0,67.9815,0) rot=(1,0,0;1.5708rad)
  Support = -> [Pad006]
  sketch-geometry (4):
    g0: LineSegment StartX=-12.6059 StartY=21.7674 StartZ=0 EndX=-17.6059 EndY=21.7674 EndZ=0
    g1: LineSegment StartX=-17.6059 StartY=21.7674 StartZ=0 EndX=-17.6059 EndY=14.7674 EndZ=0
    g2: LineSegment StartX=-17.6059 StartY=14.7674 StartZ=0 EndX=-12.6059 EndY=14.7674 EndZ=0
    g3: LineSegment StartX=-12.6059 StartY=14.7674 StartZ=0 EndX=-12.6059 EndY=21.7674 EndZ=0
  constraints (10):
    c: Coincident(g0,g1)
    c: Coincident(g1,g2)
    c: Coincident(g2,g3)
    c: Coincident(g3,g0)
    c: Horizontal(g0)
    c: Horizontal(g2)
    c: Vertical(g1)
    c: Vertical(g3)
    c: DistanceX(g0,g0) = 5
    c: DistanceY(g3,g3) = 7
FEATURE [PartDesign::Pad] Pad007
  BaseFeature = -> Pad006
  Direction = (0,-1,2e-16)
  Length = 15
  Length2 = 10
  Profile = -> Sketch008
  ReferenceAxis = -> Sketch008 [N_Axis]
  Type = 0
FEATURE [PartDesign::Pad] Pad008
  BaseFeature = -> Pad007
  Direction = (0,0,1)
  Length = 17
  Length2 = 10
  Profile = -> Pad007 [Face50]
  Type = 0
FEATURE [PartDesign::Pad] Pad009
  BaseFeature = -> Pad008
  Direction = (0,0,1)
  Length = 14
  Length2 = 10
  Profile = -> Pad008 [Face55]
  Type = 0
FEATURE [Sketcher::SketchObject] Sketch009
  FullyConstrained = false
  MapMode = 5
  Placement = pos=(0,-5.98019,0) rot=(0,0.707107,0.707107;3.14159rad)
  Support = -> [Pad009]
  sketch-geometry (4):
    g0: LineSegment StartX=-2.09996 StartY=20.7983 StartZ=0 EndX=-10.7745 EndY=20.7983 EndZ=0
    g1: LineSegment StartX=-10.7745 StartY=20.7983 StartZ=0 EndX=-10.7745 EndY=13.8581 EndZ=0
    g2: LineSegment StartX=-10.7745 StartY=13.8581 StartZ=0 EndX=-2.09996 EndY=13.8581 EndZ=0
    g3: LineSegment StartX=-2.09996 StartY=13.8581 StartZ=0 EndX=-2.09996 EndY=20.7983 EndZ=0
  constraints (8):
    c: Coincident(g0,g1)
    c: Coincident(g1,g2)
    c: Coincident(g2,g3)
    c: Coincident(g3,g0)
    c: Horizontal(g0)
    c: Horizontal(g2)
    c: Vertical(g1)
    c: Vertical(g3)
FEATURE [PartDesign::Pad] Pad010
  BaseFeature = -> Pad009
  Direction = (0,1,-2e-16)
  Length = 14
  Length2 = 10
  Profile = -> Sketch009
  ReferenceAxis = -> Sketch009 [N_Axis]
  Type = 0
FEATURE [PartDesign::Pad] Pad011
  BaseFeature = -> Pad010
  Direction = (0,0,1)
  Length = 14
  Length2 = 10
  Profile = -> Pad010 [Face69]
  Type = 0
FEATURE [Sketcher::SketchObject] Sketch010
  FullyConstrained = false
  MapMode = 5
  Support = -> [XY_Plane047]
  sketch-geometry (4):
    g0: LineSegment StartX=-64.0162 StartY=72.5506 StartZ=0 EndX=86.0943 EndY=72.5506 EndZ=0
    g1: LineSegment StartX=86.0943 StartY=72.5506 StartZ=0 EndX=86.0943 EndY=-72.5297 EndZ=0
    g2: LineSegment StartX=86.0943 StartY=-72.5297 StartZ=0 EndX=-64.0162 EndY=-72.5297 EndZ=0
    g3: LineSegment StartX=-64.0162 StartY=-72.5297 StartZ=0 EndX=-64.0162 EndY=72.5506 EndZ=0
  constraints (8):
    c: Coincident(g0,g1)
    c: Coincident(g1,g2)
    c: Coincident(g2,g3)
    c: Coincident(g3,g0)
    c: Horizontal(g0)
    c: Horizontal(g2)
    c: Vertical(g1)
    c: Vertical(g3)
FEATURE [PartDesign::Pad] Pad012
  Direction = (0,0,1)
  Length = 58
  Length2 = 10
  Profile = -> Sketch010
  ReferenceAxis = -> Sketch010 [N_Axis]
  Type = 0
FEATURE [PartDesign::Thickness] Thickness
  Base = -> Pad012 [Face5]
  BaseFeature = -> Pad012
  Intersection = false
  Join = 0
  Mode = 0
  SupportTransform = false
  Value = 1
FEATURE [Sketcher::SketchObject] Sketch011
  FullyConstrained = false
  MapMode = 5
  Placement = pos=(0,0,59) rot=(0,0,1;0rad)
  Support = -> [Thickness]
  sketch-geometry (4):
    g0: ArcOfCircle CenterX=-3.32373 CenterY=-6.29482 CenterZ=0 NormalX=0 NormalY=0 NormalZ=1 AngleXU=0 Radius=38.0702 StartAngle=1.12939 EndAngle=5.15379
    g1: ArcOfCircle CenterX=49.5606 CenterY=-6.29482 CenterZ=0 NormalX=0 NormalY=0 NormalZ=1 AngleXU=0 Radius=15.5267 StartAngle=5.23343 EndAngle=7.33295
    g2: LineSegment StartX=12.9403 StartY=28.1265 StartZ=0 EndX=57.2895 EndY=7.17153 EndZ=0
    g3: LineSegment StartX=12.9403 StartY=-40.7161 StartZ=0 EndX=57.2895 EndY=-19.7612 EndZ=0
  constraints (9):
    c: PointOnObject(g3,g1)
    c: Coincident(g1,g2)
    c: PointOnObject(g1,g3)
    c: Tangent(g0,g3) = -1.5708
    c: Coincident(g0,g2)
    c: Vertical(g1,g1)
    c: Vertical(g0,g0)
    c: Horizontal(g1,g0)
    c: Coincident(g1,g3)
FEATURE [PartDesign::Pocket] Pocket002
  BaseFeature = -> Thickness
  Direction = (0,0,-1)
  Length = 5
  Length2 = 5
  Profile = -> Sketch011
  ReferenceAxis = -> Sketch011 [N_Axis]
  Type = 0
FEATURE [Sketcher::SketchObject] Sketch012
  FullyConstrained = false
  MapMode = 5
  Support = -> [Pad011]
  sketch-geometry (10):
    g0: LineSegment StartX=-67.6264 StartY=-5.93697 StartZ=0 EndX=-72.6264 EndY=-5.93697 EndZ=0
    g1: LineSegment StartX=-72.6264 StartY=-5.93697 StartZ=0 EndX=-72.6264 EndY=-12.937 EndZ=0
    g2: LineSegment StartX=-72.6264 StartY=-12.937 StartZ=0 EndX=-67.6264 EndY=-12.937 EndZ=0
    g3: LineSegment StartX=-67.6264 StartY=-12.937 StartZ=0 EndX=-67.6264 EndY=-5.93697 EndZ=0
    g4: Circle CenterX=-70.1264 CenterY=-9.43697 CenterZ=0 NormalX=0 NormalY=0 NormalZ=1 AngleXU=0 Radius=1.75
    g5: LineSegment StartX=69.9076 StartY=-5.93697 StartZ=0 EndX=64.9076 EndY=-5.93697 EndZ=0
    g6: LineSegment StartX=64.9076 StartY=-5.93697 StartZ=0 EndX=64.9076 EndY=-12.937 EndZ=0
    g7: LineSegment StartX=64.9076 StartY=-12.937 StartZ=0 EndX=69.9076 EndY=-12.937 EndZ=0
    g8: LineSegment StartX=69.9076 StartY=-12.937 StartZ=0 EndX=69.9076 EndY=-5.93697 EndZ=0
    g9: Circle CenterX=67.4076 CenterY=-9.43697 CenterZ=0 NormalX=0 NormalY=0 NormalZ=1 AngleXU=0 Radius=1.75
  constraints (25):
    c: Coincident(g0,g1)
    c: Coincident(g1,g2)
    c: Coincident(g2,g3)
    c: Coincident(g3,g0)
    c: Horizontal(g0)
    c: Horizontal(g2)
    c: Vertical(g1)
    c: Vertical(g3)
    c: Symmetric(g2,g0,g4)
    c: Diameter(g4) = 3.5
    c: DistanceX(g0,g0) = 5
    c: DistanceY(g3,g3) = 7
    c: Coincident(g5,g6)
    c: Coincident(g6,g7)
    c: Coincident(g7,g8)
    c: Coincident(g8,g5)
    c: Horizontal(g5)
    c: Horizontal(g7)
    c: Vertical(g6)
    c: Vertical(g8)
    c: Symmetric(g7,g5,g9)
    c: Equal(g4,g9) = 3.5
    c: Equal(g0,g5) = 5
    c: Equal(g3,g8) = 7
    c: Horizontal(g9,g4)
FEATURE [PartDesign::Pad] Pad013
  BaseFeature = -> Pad011
  Direction = (0,0,1)
  Length = 58
  Length2 = 10
  Profile = -> Sketch012
  ReferenceAxis = -> Sketch012 [N_Axis]
  Type = 0
FEATURE [Sketcher::SketchObject] Sketch013
  FullyConstrained = false
  MapMode = 5
  Placement = pos=(0,0,59) rot=(0,0,1;0rad)
  Support = -> [Pocket002]
  sketch-geometry (2):
    g0: Circle CenterX=-59.1081 CenterY=-9.54513 CenterZ=0 NormalX=0 NormalY=0 NormalZ=1 AngleXU=0 Radius=1.7373
    g1: Circle CenterX=78.4033 CenterY=-9.46573 CenterZ=0 NormalX=0 NormalY=0 NormalZ=1 AngleXU=0 Radius=1.76002
FEATURE [PartDesign::Hole] Hole
  BaseFeature = -> Pocket002
  CustomThreadClearance = 0
  Depth = 22
  DepthType = 0
  Diameter = 3
  DrillForDepth = false
  DrillPoint = 1
  DrillPointAngle = 118
  HoleCutCountersinkAngle = 90
  HoleCutCustomValues = false
  HoleCutDepth = 0
  HoleCutDiameter = 6.1
  HoleCutType = 2
  ModelThread = false
  Profile = -> Sketch013
  Tapered = false
  TaperedAngle = 90
  ThreadClass = 0
  ThreadDepth = 22
  ThreadDepthType = 0
  ThreadDirection = 0
  ThreadFit = 0
  ThreadSize = 0
  ThreadType = 0
  Threaded = false
  UseCustomThreadClearance = false
FEATURE [PartDesign::Fillet] Fillet001
  Base = -> Pad013 [Edge1,Edge5]
  BaseFeature = -> Pad013
  Radius = 5
  SupportTransform = false
  UseAllEdges = false
FEATURE [PartDesign::Body] Body001  label="Base"
  Group = -> [Sketch,Pad,Sketch001,Pocket,Sketch003,Pad002,Sketch004,Pad003,Sketch005,Pad004,Pad006,Sketch008,Pad007,Pad008,Pad009,Sketch009,Pad010,Pad011,Sketch012,Pad013,Fillet001]
  Origin = -> Origin048
  Placement = pos=(11,0,0) rot=(0,0,1;0rad)
  Tip = -> Fillet001
FEATURE [Sketcher::SketchObject] Sketch014
  FullyConstrained = false
  MapMode = 5
  Placement = pos=(0,73.5506,0) rot=(0,0.707107,0.707107;3.14159rad)
  Support = -> [Hole]
  sketch-geometry (4):
    g0: LineSegment StartX=50.2453 StartY=47.3897 StartZ=0 EndX=38.6453 EndY=47.3897 EndZ=0
    g1: LineSegment StartX=38.6453 StartY=47.3897 StartZ=0 EndX=38.6453 EndY=26.7897 EndZ=0
    g2: LineSegment StartX=38.6453 StartY=26.7897 StartZ=0 EndX=50.2453 EndY=26.7897 EndZ=0
    g3: LineSegment StartX=50.2453 StartY=26.7897 StartZ=0 EndX=50.2453 EndY=47.3897 EndZ=0
  constraints (10):
    c: Coincident(g0,g1)
    c: Coincident(g1,g2)
    c: Coincident(g2,g3)
    c: Coincident(g3,g0)
    c: Horizontal(g0)
    c: Horizontal(g2)
    c: Vertical(g1)
    c: Vertical(g3)
    c: DistanceX(g0,g0) = 11.6
    c: DistanceY(g3,g3) = 20.6
FEATURE [PartDesign::Pocket] Pocket003
  BaseFeature = -> Hole
  Direction = (0,-1,2e-16)
  Length = 5
  Length2 = 5
  Profile = -> Sketch014
  ReferenceAxis = -> Sketch014 [N_Axis]
  Type = 0
FEATURE [Sketcher::SketchObject] Sketch015
  FullyConstrained = false
  MapMode = 5
  Placement = pos=(0,-73.5297,0) rot=(1,0,0;1.5708rad)
  Support = -> [Pocket003]
  sketch-geometry (4):
    g0: LineSegment StartX=-52.3934 StartY=19.2989 StartZ=0 EndX=-35.4731 EndY=19.2989 EndZ=0
    g1: LineSegment StartX=-35.4731 StartY=19.2989 StartZ=0 EndX=-35.4731 EndY=1.09424 EndZ=0
    g2: LineSegment StartX=-35.4731 StartY=1.09424 StartZ=0 EndX=-52.3934 EndY=1.09424 EndZ=0
    g3: LineSegment StartX=-52.3934 StartY=1.09424 StartZ=0 EndX=-52.3934 EndY=19.2989 EndZ=0
  constraints (8):
    c: Coincident(g0,g1)
    c: Coincident(g1,g2)
    c: Coincident(g2,g3)
    c: Coincident(g3,g0)
    c: Horizontal(g0)
    c: Horizontal(g2)
    c: Vertical(g1)
    c: Vertical(g3)
FEATURE [PartDesign::Pocket] Pocket004
  BaseFeature = -> Pocket003
  Direction = (0,1,-2e-16)
  Length = 5
  Length2 = 5
  Profile = -> Sketch015
  ReferenceAxis = -> Sketch015 [N_Axis]
  Type = 0
FEATURE [Sketcher::SketchObject] Sketch016
  FullyConstrained = false
  MapMode = 5
  Placement = pos=(-65.0162,0,0) rot=(0.57735,-0.57735,-0.57735;2.0944rad)
  Support = -> [Pocket004]
  sketch-geometry (8):
    g0: LineSegment StartX=-37.7946 StartY=49.8014 StartZ=0 EndX=38.411 EndY=49.8014 EndZ=0
    g1: LineSegment StartX=39.2068 StartY=49.0055 StartZ=0 EndX=39.2068 EndY=46.8415 EndZ=0
    g2: LineSegment StartX=38.1667 StartY=45.8014 StartZ=0 EndX=-37.6283 EndY=45.8014 EndZ=0
    g3: LineSegment StartX=-38.8512 StartY=47.0243 StartZ=0 EndX=-38.8512 EndY=48.7447 EndZ=0
    g4: ArcOfCircle CenterX=-37.7946 CenterY=48.7447 CenterZ=0 NormalX=0 NormalY=0 NormalZ=1 AngleXU=0 Radius=1.05665 StartAngle=1.5708 EndAngle=3.14159
    g5: ArcOfCircle CenterX=-37.6283 CenterY=47.0243 CenterZ=0 NormalX=0 NormalY=0 NormalZ=1 AngleXU=0 Radius=1.2229 StartAngle=3.14159 EndAngle=4.71239
    g6: ArcOfCircle CenterX=38.411 CenterY=49.0055 CenterZ=0 NormalX=0 NormalY=0 NormalZ=1 AngleXU=0 Radius=0.795866 StartAngle=0 EndAngle=1.5708
    g7: ArcOfCircle CenterX=38.1667 CenterY=46.8415 CenterZ=0 NormalX=0 NormalY=0 NormalZ=1 AngleXU=0 Radius=1.04015 StartAngle=4.71239 EndAngle=6.28319
  constraints (12):
    c: Horizontal(g0)
    c: Horizontal(g2)
    c: Vertical(g1)
    c: Vertical(g3)
    c: Tangent(g3,g4) = 1.5708
    c: Tangent(g0,g4) = 1.5708
    c: Tangent(g2,g5) = 1.5708
    c: Tangent(g3,g5) = 1.5708
    c: Tangent(g1,g6) = 1.5708
    c: Tangent(g0,g6) = 1.5708
    c: Tangent(g2,g7) = 1.5708
    c: Tangent(g1,g7) = 1.5708
FEATURE [PartDesign::Pocket] Pocket005
  BaseFeature = -> Pocket004
  Direction = (1,0,0)
  Length = 5
  Length2 = 5
  Profile = -> Sketch016
  ReferenceAxis = -> Sketch016 [N_Axis]
  Type = 0
FEATURE [Sketcher::SketchObject] Sketch017
  FullyConstrained = false
  MapMode = 5
  Placement = pos=(0,-73.5297,0) rot=(1,0,0;1.5708rad)
  sketch-geometry (5):
    g0: Circle CenterX=-26.672 CenterY=43.2708 CenterZ=0 NormalX=0 NormalY=0 NormalZ=1 AngleXU=0 Radius=1.5
    g1: Circle CenterX=-3.17201 CenterY=43.2708 CenterZ=0 NormalX=0 NormalY=0 NormalZ=1 AngleXU=0 Radius=1.5
    g2: Circle CenterX=-26.672 CenterY=19.7708 CenterZ=0 NormalX=0 NormalY=0 NormalZ=1 AngleXU=0 Radius=1.5
    g3: Circle CenterX=-3.17201 CenterY=19.7708 CenterZ=0 NormalX=0 NormalY=0 NormalZ=1 AngleXU=0 Radius=1.5
    g4: Circle CenterX=-14.922 CenterY=31.5208 CenterZ=0 NormalX=0 NormalY=0 NormalZ=1 AngleXU=0 Radius=12.5
  constraints (12):
    c: Symmetric(g0,g3,g4)
    c: Horizontal(g1,g0)
    c: Vertical(g2,g0)
    c: Horizontal(g3,g2)
    c: Vertical(g3,g1)
    c: Diameter(g0) = 3
    c: Equal(g0,g1)
    c: Equal(g2,g0)
    c: Equal(g0,g3)
    c: DistanceX(g0,g1) = 23.5
    c: DistanceY(g2,g0) = 23.5
    c: Diameter(g4) = 25
FEATURE [PartDesign::Pocket] Pocket006
  BaseFeature = -> Pocket005
  Direction = (0,1,-2e-16)
  Length = 5
  Length2 = 5
  Profile = -> Sketch017
  ReferenceAxis = -> Sketch017 [N_Axis]
  Type = 0
FEATURE [PartDesign::LinearPattern] LinearPattern
  Direction = -> Z_Axis047
  Length = 30
  Occurrences = 4
  Reversed = true
FEATURE [PartDesign::MultiTransform] MultiTransform
  BaseFeature = -> Pocket006
  Originals = -> [Pocket005]
  Transformations = -> [LinearPattern]
FEATURE [Sketcher::SketchObject] Sketch018
  FullyConstrained = false
  MapMode = 5
  Placement = pos=(87.0943,0,0) rot=(0.57735,0.57735,0.57735;2.0944rad)
  Support = -> [MultiTransform]
  sketch-geometry (7):
    g0: LineSegment StartX=-55.8115 StartY=45.8138 StartZ=0 EndX=-54.3336 EndY=48.3737 EndZ=0
    g1: LineSegment StartX=-54.3336 StartY=48.3737 StartZ=0 EndX=-55.8115 EndY=50.9337 EndZ=0
    g2: LineSegment StartX=-55.8115 StartY=50.9337 StartZ=0 EndX=-58.7675 EndY=50.9337 EndZ=0
    g3: LineSegment StartX=-58.7675 StartY=50.9337 StartZ=0 EndX=-60.2455 EndY=48.3737 EndZ=0
    g4: LineSegment StartX=-60.2455 StartY=48.3737 StartZ=0 EndX=-58.7675 EndY=45.8138 EndZ=0
    g5: LineSegment StartX=-58.7675 StartY=45.8138 StartZ=0 EndX=-55.8115 EndY=45.8138 EndZ=0
    g6: Circle CenterX=-57.2895 CenterY=48.3737 CenterZ=0 NormalX=0 NormalY=0 NormalZ=1 AngleXU=0 Radius=2.95595
  constraints (14):
    c: Coincident(g0,g1)
    c: Coincident(g1,g2)
    c: Coincident(g2,g3)
    c: Coincident(g3,g4)
    c: Coincident(g4,g5)
    c: Coincident(g5,g0)
    c: Equal(g0, g1-g5) x5
    c: PointOnObject(g0,g6)
    c: PointOnObject(g1,g6)
    c: PointOnObject(g2,g6)
    c: PointOnObject(g3,g6)
    c: PointOnObject(g4,g6)
    c: PointOnObject(g5,g6)
    c: Horizontal(g5)
FEATURE [PartDesign::Pocket] Pocket007
  BaseFeature = -> MultiTransform
  Direction = (-1,0,0)
  Length = 5
  Length2 = 5
  Profile = -> Sketch018
  ReferenceAxis = -> Sketch018 [N_Axis]
  Type = 0
FEATURE [PartDesign::LinearPattern] LinearPattern001
  Direction = -> Sketch018 [H_Axis]
  Length = 150
  Occurrences = 10
FEATURE [PartDesign::LinearPattern] LinearPattern002
  Direction = -> Z_Axis047
  Length = 40
  Occurrences = 4
  Reversed = true
FEATURE [PartDesign::MultiTransform] MultiTransform001
  BaseFeature = -> Pocket007
  Originals = -> [Pocket007]
  Transformations = -> [LinearPattern001,LinearPattern002]
FEATURE [PartDesign::Body] Body  label="Cover"
  Group = -> [Sketch010,Pad012,Thickness,Sketch011,Pocket002,Sketch013,Hole,Sketch014,Pocket003,Sketch015,Pocket004,Sketch016,Pocket005,Sketch017,Pocket006,MultiTransform,LinearPattern,Sketch018,Pocket007,MultiTransform001,LinearPattern001,LinearPattern002]
  Origin = -> Origin047
  Tip = -> MultiTransform001
FEATURE [App::Part] Part  label="Robot Design"
  Group = -> [Body,Body001,Body003]
  Origin = -> Origin
